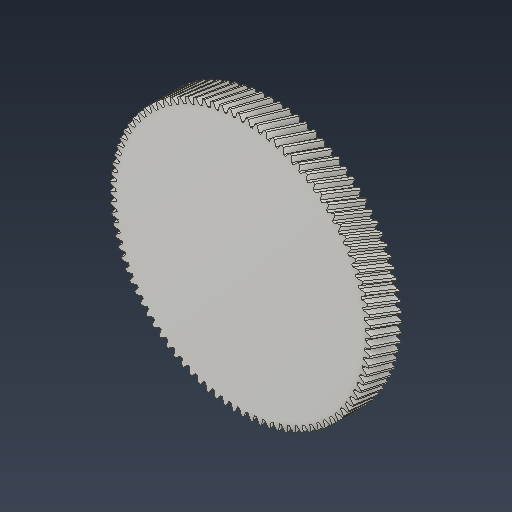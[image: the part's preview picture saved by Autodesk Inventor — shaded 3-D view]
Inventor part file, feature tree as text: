
AUTODESK INVENTOR PART (.ipt)
format: ipt  version: 2022 (Build 260153000, 153)  size: 1,141,248 bytes
history: native  units: mm (DEFAULTED — no unit token found)
features: plane x3, other x3, sketch x2, extrude x1
ambient origin geometry x8: Origin, YZ Plane, XZ Plane, XY Plane, X Axis, Y Axis, Z Axis, Center Point
bodies: Solid1 (feature_tree)
feature tree (9):
  extrude  "Extrusion1"  Depth=20.0mm TaperAngle=0.0deg
  plane  "Work Plane2"
  plane  "Work Plane8"
  plane  "Work Plane9"
  other  "Spur Gear"
  sketch  "Sketch1"  dims[d0=168.666845mm d1=20.0mm d2=0.0mm]
  sketch  "Sketch2"  dims[d3=171.332621mm d4=10.0mm d5=0.0mm d16=104.0mm d17=0.0mm d34=0.341477mm d39=0.0mm d41=0.0mm d43=104.0mm d46=104.0mm d47=0.0mm d48=0.0mm]
  other  "Srf1"
  other  "Pitch Diameter"
